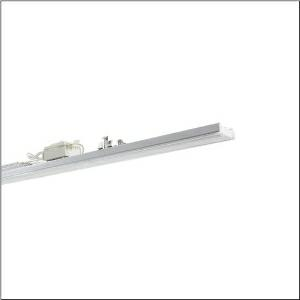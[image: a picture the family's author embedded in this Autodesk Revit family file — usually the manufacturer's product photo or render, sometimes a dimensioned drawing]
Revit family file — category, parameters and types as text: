
# Revit family: licross_21_recessed_mo_52tl14mn4axg
name_source: partatom
category: Lighting Fixtures
units: mm (PartAtom-declared; Revit-internal decimal feet)

## family parameters
Cut with Voids When Loaded = No
Host = Face
Light Source = No
Part Type = Normal
Room Calculation Point = No
Round Connector Dimension = Use Diameter
Shared = No

## types (1)
- --- (1 x LED, 10120 lm, 60.5 W, 4000K)
    Apparent Load = 61 VA
    CIE Flux Codes = 56 84 97 100 100
    Color Rendering = 80
    Color Temperature = 4000K
    Default Elevation = 1800 mm
    Description = Licross 21 Recessed MO, luminaire insert, of sheet steel, galvanised, coil coated, white, length: 1.500mm, width: 66mm, height: 67mm, LED rated luminous flux: 10.120lm, light colour: 840, SDCM (Standard Deviation of Colour Matching)MacAdam ≤ 3 SDCM (initial), control gear: ON/OFF Multilumen, with plug, 3-pole, with phase selection, mains connection: 220..240V, AC, 50/60Hz, rated input power: 61W, internal wiring halogen-free, primary light control with lens, of plastic, primary optical cover: cover, of PMMA, light emission: direct distribution, primary light characteristic: asymmetric, protection rating (complete): IP40, insulation class (complete): insulation class I (protective earthing), certification: CE, ENEC, VDE, UKCA, protection symbol: D if used in an environment without relevant dust loads with corresponding accessories, impact resistance: IK06, permissible ambient temperature for indoor applications: -35..+40°C, corresponds to IFS (International Featured Standards) requirements for safety and quality in the food industry, reducing of maximum allowable ambient temperature of 5°C with ceiling mounting, LABS conformity tested according to VDMA 24364:2018-05, The light source and the operating device comply with the requirements of the Ecodesign Regulation (EU) 2019/2020 and are replaceable in accordance with this regulation, packaging unit: 1 piece
    Height = 58 mm
    Lamp = 1 x LED
    Lamp Light Flux = 10120 lm
    Lamp Power = 60.5 W
    Lamp count = 1
    Length = 1500 mm
    Luminous efficacy = 167 lm/W
    Manufacturer = Siteco
    ModVariant = No
    Model = 52TL14MN4AXG
    Mounting Place = Ceiling
    Mounting Type = Pendant
    Number of Poles = 1
    OnlyDefault = Yes
    Power Factor = 1
    Product Name = Licross 21 Recessed MO
    Product group = luminaire insert | ceiling pendant
    ProductGroupID = 901
    Protection Class = Protection class I
    Protection Degree = IP 40
    RLX_Detail_Level = 1
    RLX_Emergency_Light_Flux = 0 lm
    RLX_Emergency_Type = 0
    RLX_Emergency_Type_DB = No
    RlxData = <blob elided: 23009 chars, md5=46cd801f>
    Socket = socket
    Standby Power = 0 W
    System Light Flux = 10120 lm
    System Power = 61 W
    Type Comments = factory setting: luminous flux: 100 % | (A | C | E) | 140 mA
    Type Image = l_1296930.jpg
    URL = http://relux.com
    VarID = @adj_108043
    Voltage = 0 V
    Weight = 0.00 kg
    Width = 66 mm

## geometry (parser evidence)
native form markers: Blend x4, Sweep x10
no freeform markers — native parametric forms only
